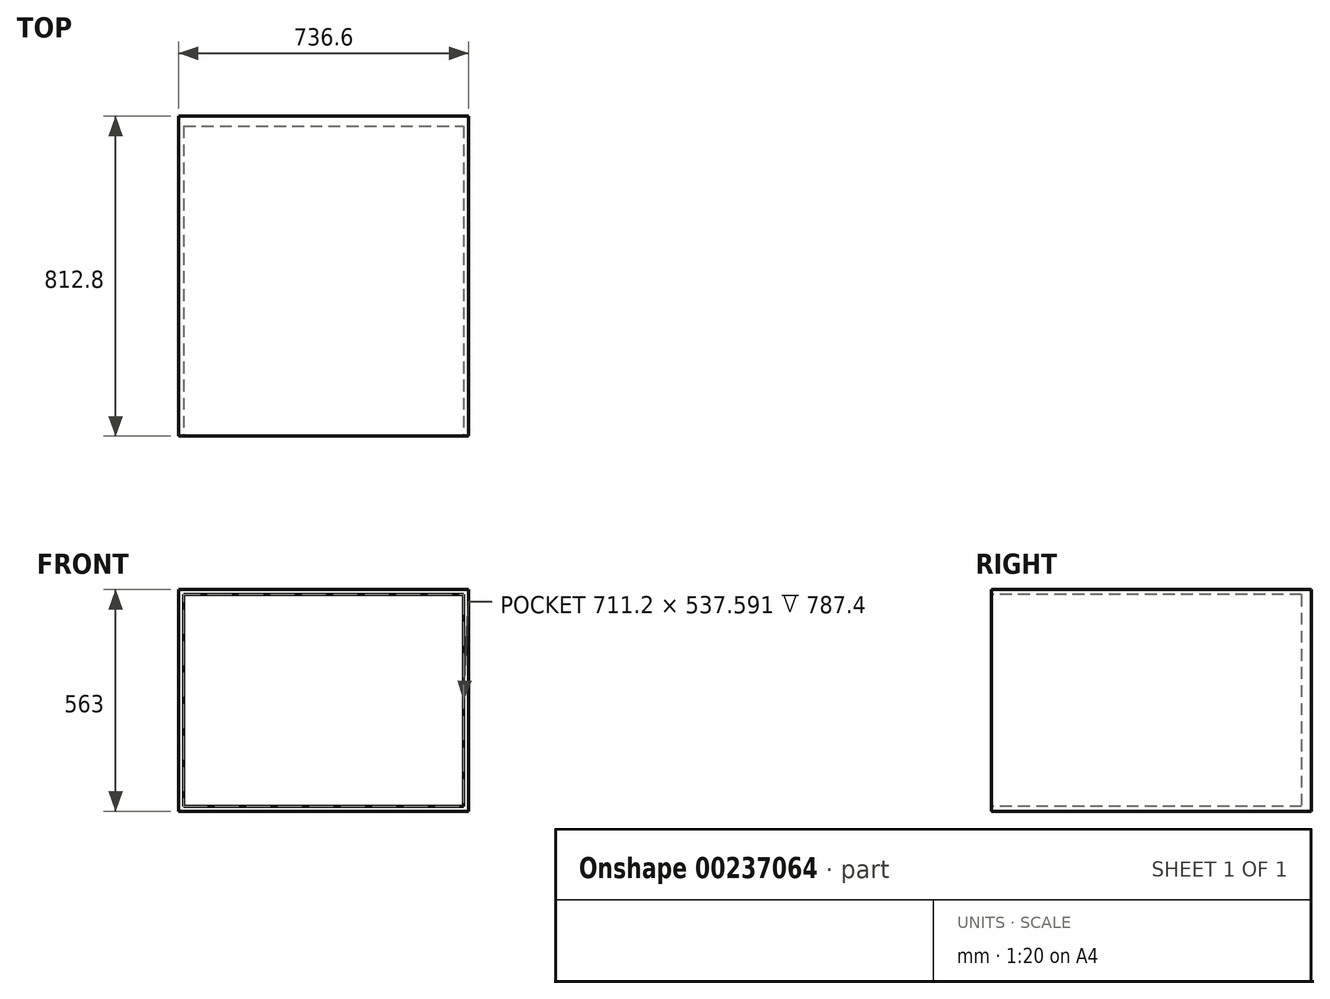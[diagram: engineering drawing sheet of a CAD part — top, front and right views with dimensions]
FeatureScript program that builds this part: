
annotation { "Feature Type Name" : "Feature", "Feature Type Description" : "" }
export const myFeature = defineFeature(function(context is Context, id is Id, definition is map)
    precondition{}
    {
        {
            var Q0;
            Q0=qCreatedBy(makeId("Front.planeOp"),FACE);
            var sketch = newSketch(context, id + "F0", { "sketchPlane" : qUnion([Q0])});
            skLineSegment(sketch, "E0.bottom", {"start": v(-368.3, 281.5) * mm, "end": v(368.3, 281.5) * mm});
            skLineSegment(sketch, "E0.top", {"start": v(-368.3, -281.5) * mm, "end": v(368.3, -281.5) * mm});
            skLineSegment(sketch, "E0.left", {"start": v(-368.3, 281.5) * mm, "end": v(-368.3, -281.5) * mm});
            skLineSegment(sketch, "E0.right", {"start": v(368.3, 281.5) * mm, "end": v(368.3, -281.5) * mm});
            skPoint(sketch, "E0.middle", {"position": v(0, 0) * mm});
            skLineSegment(sketch, "E1.bottom", {"start": v(-355.6, 268.8) * mm, "end": v(355.6, 268.8) * mm});
            skLineSegment(sketch, "E1.top", {"start": v(-355.6, -268.8) * mm, "end": v(355.6, -268.8) * mm});
            skLineSegment(sketch, "E1.left", {"start": v(-355.6, 268.8) * mm, "end": v(-355.6, -268.8) * mm});
            skLineSegment(sketch, "E1.right", {"start": v(355.6, 268.8) * mm, "end": v(355.6, -268.8) * mm});
            skSolve(sketch);
        }
        {
            var Q0;
            Q0=makeQuery(id+"F0.imprint","IMPRINT",FACE,{"disambiguationData":[TD([[makeQuery(id+"F0.imprint","IMPRINT",EDGE,{"derivedFrom":sQuery(id+"F0.wireOp",EDGE,"E0.bottom")}),-1.0]])]});
            var Q1;
            Q1=makeQuery(id+"F0.imprint","IMPRINT",FACE,{"disambiguationData":[TD([[makeQuery(id+"F0.imprint","IMPRINT",EDGE,{"derivedFrom":sQuery(id+"F0.wireOp",EDGE,"E1.bottom")}),-1.0]])]});
            extrude(context, id + "F1", {"entities" : qUnion([Q0, Q1]), "oppositeDirection" : true, "depth" : 812.8 * mm});
        }
        {
            var Q0;
            Q0=makeQuery(id+"F0.imprint","IMPRINT",FACE,{"disambiguationData":[TD([[makeQuery(id+"F0.imprint","IMPRINT",EDGE,{"derivedFrom":sQuery(id+"F0.wireOp",EDGE,"E1.bottom")}),-1.0]])]});
            extrude(context, id + "F2", {"entities" : qUnion([Q0]), "operationType" : NewBodyOperationType.REMOVE, "oppositeDirection" : true, "depth" : 787.4 * mm});
        }
    });
